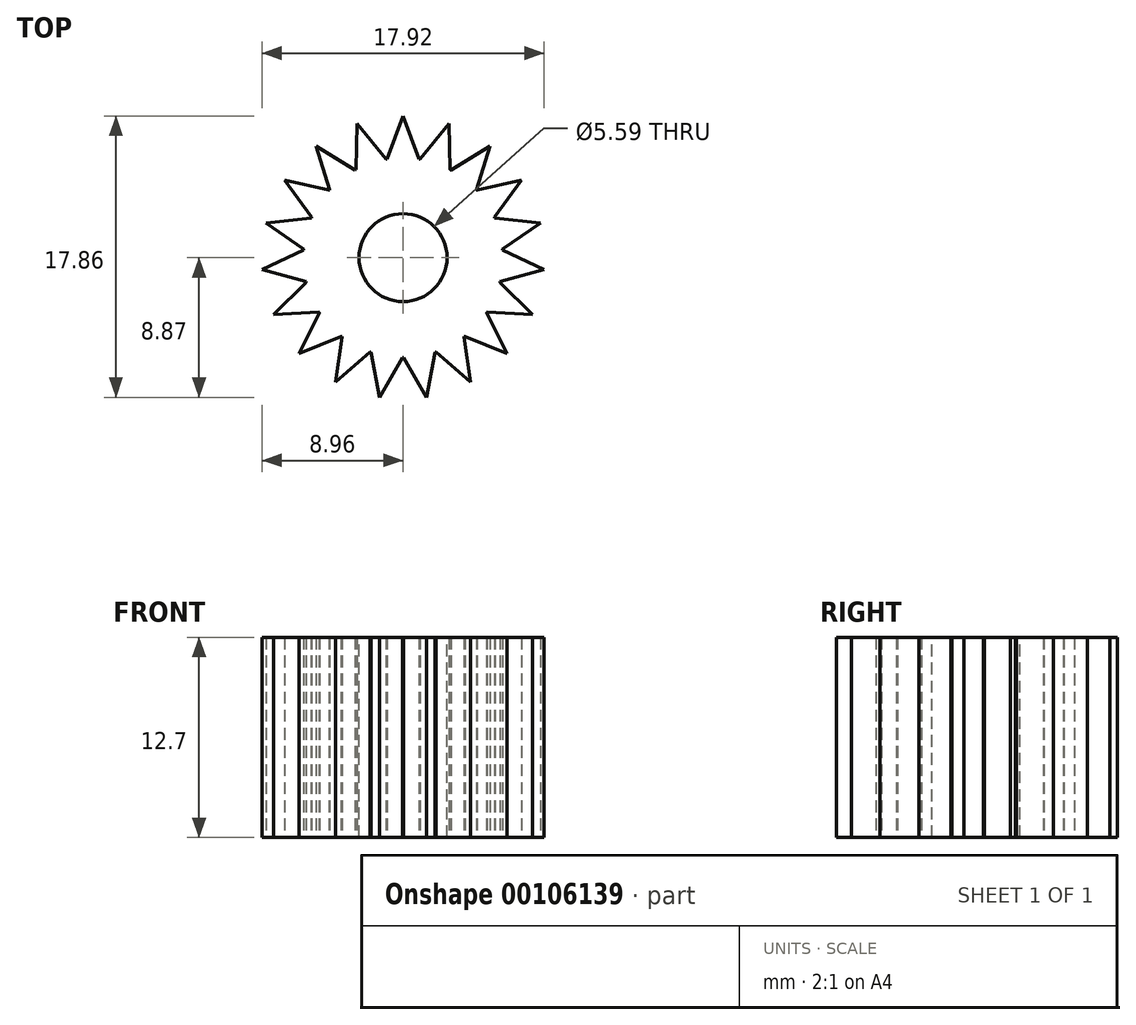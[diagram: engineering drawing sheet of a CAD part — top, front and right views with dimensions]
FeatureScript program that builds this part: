
annotation { "Feature Type Name" : "Feature", "Feature Type Description" : "" }
export const myFeature = defineFeature(function(context is Context, id is Id, definition is map)
    precondition{}
    {
        {
            var Q0;
            Q0=qCreatedBy(makeId("Top.planeOp"),FACE);
            var sketch = newSketch(context, id + "F0", { "sketchPlane" : qUnion([Q0])});
            skCircle(sketch, "E0", {"center": v(0, 0) * mm, "radius": 6.35 * mm});
            skLineSegment(sketch, "E1", {"start": v(-1.02, 6.27) * mm, "end": v(0, 9) * mm});
            skLineSegment(sketch, "E2", {"start": v(0, 9) * mm, "end": v(1.02, 6.27) * mm});
            skLineSegment(sketch, "E3.1.0", {"start": v(-3, 5.6) * mm, "end": v(-2.92, 8.5) * mm});
            skLineSegment(sketch, "E3.1.1", {"start": v(-2.92, 8.5) * mm, "end": v(-1.07, 6.26) * mm});
            skLineSegment(sketch, "E3.2.0", {"start": v(-4.65, 4.32) * mm, "end": v(-5.52, 7.1) * mm});
            skLineSegment(sketch, "E3.2.1", {"start": v(-5.52, 7.1) * mm, "end": v(-3.05, 5.57) * mm});
            skLineSegment(sketch, "E3.3.0", {"start": v(-5.8, 2.58) * mm, "end": v(-7.53, 4.92) * mm});
            skLineSegment(sketch, "E3.3.1", {"start": v(-7.53, 4.92) * mm, "end": v(-4.7, 4.28) * mm});
            skLineSegment(sketch, "E3.4.0", {"start": v(-6.33, 0.55) * mm, "end": v(-8.72, 2.2) * mm});
            skLineSegment(sketch, "E3.4.1", {"start": v(-8.72, 2.2) * mm, "end": v(-5.83, 2.52) * mm});
            skLineSegment(sketch, "E3.5.0", {"start": v(-6.16, -1.53) * mm, "end": v(-8.96, -0.74) * mm});
            skLineSegment(sketch, "E3.5.1", {"start": v(-8.96, -0.74) * mm, "end": v(-6.33, 0.5) * mm});
            skLineSegment(sketch, "E3.6.0", {"start": v(-5.33, -3.45) * mm, "end": v(-8.23, -3.61) * mm});
            skLineSegment(sketch, "E3.6.1", {"start": v(-8.23, -3.61) * mm, "end": v(-6.15, -1.59) * mm});
            skLineSegment(sketch, "E3.7.0", {"start": v(-3.92, -5) * mm, "end": v(-6.61, -6.09) * mm});
            skLineSegment(sketch, "E3.7.1", {"start": v(-6.61, -6.09) * mm, "end": v(-5.3, -3.5) * mm});
            skLineSegment(sketch, "E3.8.0", {"start": v(-2.09, -6) * mm, "end": v(-4.28, -7.9) * mm});
            skLineSegment(sketch, "E3.8.1", {"start": v(-4.28, -7.9) * mm, "end": v(-3.88, -5.03) * mm});
            skLineSegment(sketch, "E3.9.0", {"start": v(-0.03, -6.35) * mm, "end": v(-1.48, -8.87) * mm});
            skLineSegment(sketch, "E3.9.1", {"start": v(-1.48, -8.87) * mm, "end": v(-2.03, -6.02) * mm});
            skLineSegment(sketch, "E4.1.10.0", {"start": v(2.03, -6.02) * mm, "end": v(1.48, -8.87) * mm});
            skLineSegment(sketch, "E4.3.10.0", {"start": v(1.48, -8.87) * mm, "end": v(0.03, -6.35) * mm});
            skLineSegment(sketch, "E4.1.11.0", {"start": v(3.88, -5.03) * mm, "end": v(4.28, -7.9) * mm});
            skLineSegment(sketch, "E4.3.11.0", {"start": v(4.28, -7.9) * mm, "end": v(2.09, -6) * mm});
            skLineSegment(sketch, "E5.1.12.0", {"start": v(5.3, -3.5) * mm, "end": v(6.61, -6.09) * mm});
            skLineSegment(sketch, "E5.3.12.0", {"start": v(6.61, -6.09) * mm, "end": v(3.92, -5) * mm});
            skLineSegment(sketch, "E5.1.13.0", {"start": v(6.15, -1.59) * mm, "end": v(8.23, -3.61) * mm});
            skLineSegment(sketch, "E5.3.13.0", {"start": v(8.23, -3.61) * mm, "end": v(5.33, -3.45) * mm});
            skLineSegment(sketch, "E6.1.14.0", {"start": v(6.33, 0.5) * mm, "end": v(8.96, -0.74) * mm});
            skLineSegment(sketch, "E6.3.14.0", {"start": v(8.96, -0.74) * mm, "end": v(6.16, -1.53) * mm});
            skLineSegment(sketch, "E6.1.15.0", {"start": v(5.83, 2.52) * mm, "end": v(8.72, 2.2) * mm});
            skLineSegment(sketch, "E6.3.15.0", {"start": v(8.72, 2.2) * mm, "end": v(6.33, 0.55) * mm});
            skLineSegment(sketch, "E7.1.16.0", {"start": v(4.7, 4.28) * mm, "end": v(7.53, 4.92) * mm});
            skLineSegment(sketch, "E7.3.16.0", {"start": v(7.53, 4.92) * mm, "end": v(5.8, 2.58) * mm});
            skLineSegment(sketch, "E7.1.17.0", {"start": v(3.05, 5.57) * mm, "end": v(5.52, 7.1) * mm});
            skLineSegment(sketch, "E7.3.17.0", {"start": v(5.52, 7.1) * mm, "end": v(4.65, 4.32) * mm});
            skLineSegment(sketch, "E8.1.18.0", {"start": v(1.07, 6.26) * mm, "end": v(2.92, 8.5) * mm});
            skLineSegment(sketch, "E8.3.18.0", {"start": v(2.92, 8.5) * mm, "end": v(3, 5.6) * mm});
            skSolve(sketch);
        }
        {
            var Q0;
            {var subQ0=sQuery(id+"F0.wireOp",EDGE,"E0");var subQ27=makeQuery(id+"F0.imprint","INTERSECT",VERTEX,{"derivedFrom":[subQ0,sQuery(id+"F0.wireOp",EDGE,"E6.1.14.0")]});Q0=makeQuery(id+"F0.imprint","IMPRINT",FACE,{"disambiguationData":[TD([[makeQuery(id+"F0.imprint","IMPRINT",EDGE,{"disambiguationData":[TD([[subQ27,-1.0]])],"derivedFrom":subQ0}),1.0]])]});}
            var Q1;
            {var subQ0=sQuery(id+"F0.wireOp",EDGE,"E8.1.18.0");Q1=makeQuery(id+"F0.imprint","IMPRINT",FACE,{"disambiguationData":[TD([[makeQuery(id+"F0.imprint","IMPRINT",EDGE,{"derivedFrom":subQ0}),-1.0]])]});}
            var Q2;
            {var subQ0=sQuery(id+"F0.wireOp",EDGE,"E3.4.0");Q2=makeQuery(id+"F0.imprint","IMPRINT",FACE,{"disambiguationData":[TD([[makeQuery(id+"F0.imprint","IMPRINT",EDGE,{"derivedFrom":subQ0}),-1.0]])]});}
            var Q3;
            {var subQ0=sQuery(id+"F0.wireOp",EDGE,"E3.2.0");Q3=makeQuery(id+"F0.imprint","IMPRINT",FACE,{"disambiguationData":[TD([[makeQuery(id+"F0.imprint","IMPRINT",EDGE,{"derivedFrom":subQ0}),-1.0]])]});}
            var Q4;
            {var subQ0=sQuery(id+"F0.wireOp",EDGE,"E6.1.15.0");Q4=makeQuery(id+"F0.imprint","IMPRINT",FACE,{"disambiguationData":[TD([[makeQuery(id+"F0.imprint","IMPRINT",EDGE,{"derivedFrom":subQ0}),-1.0]])]});}
            var Q5;
            {var subQ0=sQuery(id+"F0.wireOp",EDGE,"E6.1.14.0");Q5=makeQuery(id+"F0.imprint","IMPRINT",FACE,{"disambiguationData":[TD([[makeQuery(id+"F0.imprint","IMPRINT",EDGE,{"derivedFrom":subQ0}),-1.0]])]});}
            var Q6;
            {var subQ0=sQuery(id+"F0.wireOp",EDGE,"E5.1.13.0");Q6=makeQuery(id+"F0.imprint","IMPRINT",FACE,{"disambiguationData":[TD([[makeQuery(id+"F0.imprint","IMPRINT",EDGE,{"derivedFrom":subQ0}),-1.0]])]});}
            var Q7;
            {var subQ0=sQuery(id+"F0.wireOp",EDGE,"E3.8.0");Q7=makeQuery(id+"F0.imprint","IMPRINT",FACE,{"disambiguationData":[TD([[makeQuery(id+"F0.imprint","IMPRINT",EDGE,{"derivedFrom":subQ0}),-1.0]])]});}
            var Q8;
            {var subQ0=sQuery(id+"F0.wireOp",EDGE,"E3.7.0");Q8=makeQuery(id+"F0.imprint","IMPRINT",FACE,{"disambiguationData":[TD([[makeQuery(id+"F0.imprint","IMPRINT",EDGE,{"derivedFrom":subQ0}),-1.0]])]});}
            var Q9;
            {var subQ0=sQuery(id+"F0.wireOp",EDGE,"E3.5.0");Q9=makeQuery(id+"F0.imprint","IMPRINT",FACE,{"disambiguationData":[TD([[makeQuery(id+"F0.imprint","IMPRINT",EDGE,{"derivedFrom":subQ0}),-1.0]])]});}
            var Q10;
            {var subQ0=sQuery(id+"F0.wireOp",EDGE,"E3.3.0");Q10=makeQuery(id+"F0.imprint","IMPRINT",FACE,{"disambiguationData":[TD([[makeQuery(id+"F0.imprint","IMPRINT",EDGE,{"derivedFrom":subQ0}),-1.0]])]});}
            var Q11;
            {var subQ0=sQuery(id+"F0.wireOp",EDGE,"E3.1.0");Q11=makeQuery(id+"F0.imprint","IMPRINT",FACE,{"disambiguationData":[TD([[makeQuery(id+"F0.imprint","IMPRINT",EDGE,{"derivedFrom":subQ0}),-1.0]])]});}
            var Q12;
            {var subQ0=sQuery(id+"F0.wireOp",EDGE,"E1");Q12=makeQuery(id+"F0.imprint","IMPRINT",FACE,{"disambiguationData":[TD([[makeQuery(id+"F0.imprint","IMPRINT",EDGE,{"derivedFrom":subQ0}),-1.0]])]});}
            var Q13;
            {var subQ0=sQuery(id+"F0.wireOp",EDGE,"E7.1.17.0");Q13=makeQuery(id+"F0.imprint","IMPRINT",FACE,{"disambiguationData":[TD([[makeQuery(id+"F0.imprint","IMPRINT",EDGE,{"derivedFrom":subQ0}),-1.0]])]});}
            var Q14;
            {var subQ0=sQuery(id+"F0.wireOp",EDGE,"E4.1.10.0");Q14=makeQuery(id+"F0.imprint","IMPRINT",FACE,{"disambiguationData":[TD([[makeQuery(id+"F0.imprint","IMPRINT",EDGE,{"derivedFrom":subQ0}),-1.0]])]});}
            var Q15;
            {var subQ0=sQuery(id+"F0.wireOp",EDGE,"E3.9.0");Q15=makeQuery(id+"F0.imprint","IMPRINT",FACE,{"disambiguationData":[TD([[makeQuery(id+"F0.imprint","IMPRINT",EDGE,{"derivedFrom":subQ0}),-1.0]])]});}
            var Q16;
            {var subQ0=sQuery(id+"F0.wireOp",EDGE,"E4.1.11.0");Q16=makeQuery(id+"F0.imprint","IMPRINT",FACE,{"disambiguationData":[TD([[makeQuery(id+"F0.imprint","IMPRINT",EDGE,{"derivedFrom":subQ0}),-1.0]])]});}
            var Q17;
            {var subQ0=sQuery(id+"F0.wireOp",EDGE,"E5.1.12.0");Q17=makeQuery(id+"F0.imprint","IMPRINT",FACE,{"disambiguationData":[TD([[makeQuery(id+"F0.imprint","IMPRINT",EDGE,{"derivedFrom":subQ0}),-1.0]])]});}
            var Q18;
            {var subQ0=sQuery(id+"F0.wireOp",EDGE,"E7.1.16.0");Q18=makeQuery(id+"F0.imprint","IMPRINT",FACE,{"disambiguationData":[TD([[makeQuery(id+"F0.imprint","IMPRINT",EDGE,{"derivedFrom":subQ0}),-1.0]])]});}
            var Q19;
            {var subQ0=sQuery(id+"F0.wireOp",EDGE,"E3.6.0");Q19=makeQuery(id+"F0.imprint","IMPRINT",FACE,{"disambiguationData":[TD([[makeQuery(id+"F0.imprint","IMPRINT",EDGE,{"derivedFrom":subQ0}),-1.0]])]});}
            extrude(context, id + "F1", {"entities" : qUnion([Q0, Q1, Q2, Q3, Q4, Q5, Q6, Q7, Q8, Q9, Q10, Q11, Q12, Q13, Q14, Q15, Q16, Q17, Q18, Q19]), "depth" : 12.7 * mm});
        }
        {
            var Q0;
            Q0=makeQuery(id+"F1.opExtrude","CAP_FACE",FACE,{"disambiguationData":[OSD([sQuery(id+"F0.wireOp",EDGE,"E0"),sQuery(id+"F0.wireOp",EDGE,"E1"),sQuery(id+"F0.wireOp",EDGE,"E2"),sQuery(id+"F0.wireOp",EDGE,"E3.1.0"),sQuery(id+"F0.wireOp",EDGE,"E3.1.1"),sQuery(id+"F0.wireOp",EDGE,"E3.2.0"),sQuery(id+"F0.wireOp",EDGE,"E3.2.1"),sQuery(id+"F0.wireOp",EDGE,"E3.3.0"),sQuery(id+"F0.wireOp",EDGE,"E3.3.1"),sQuery(id+"F0.wireOp",EDGE,"E3.4.0"),sQuery(id+"F0.wireOp",EDGE,"E3.4.1"),sQuery(id+"F0.wireOp",EDGE,"E3.5.0"),sQuery(id+"F0.wireOp",EDGE,"E3.5.1"),sQuery(id+"F0.wireOp",EDGE,"E3.6.0"),sQuery(id+"F0.wireOp",EDGE,"E3.6.1"),sQuery(id+"F0.wireOp",EDGE,"E3.7.0"),sQuery(id+"F0.wireOp",EDGE,"E3.7.1"),sQuery(id+"F0.wireOp",EDGE,"E3.8.0"),sQuery(id+"F0.wireOp",EDGE,"E3.8.1"),sQuery(id+"F0.wireOp",EDGE,"E3.9.0"),sQuery(id+"F0.wireOp",EDGE,"E3.9.1"),sQuery(id+"F0.wireOp",EDGE,"E4.1.10.0"),sQuery(id+"F0.wireOp",EDGE,"E4.3.10.0"),sQuery(id+"F0.wireOp",EDGE,"E4.1.11.0"),sQuery(id+"F0.wireOp",EDGE,"E4.3.11.0"),sQuery(id+"F0.wireOp",EDGE,"E5.1.12.0"),sQuery(id+"F0.wireOp",EDGE,"E5.3.12.0"),sQuery(id+"F0.wireOp",EDGE,"E5.1.13.0"),sQuery(id+"F0.wireOp",EDGE,"E5.3.13.0"),sQuery(id+"F0.wireOp",EDGE,"E6.1.14.0"),sQuery(id+"F0.wireOp",EDGE,"E6.3.14.0"),sQuery(id+"F0.wireOp",EDGE,"E6.1.15.0"),sQuery(id+"F0.wireOp",EDGE,"E6.3.15.0"),sQuery(id+"F0.wireOp",EDGE,"E7.1.16.0"),sQuery(id+"F0.wireOp",EDGE,"E7.3.16.0"),sQuery(id+"F0.wireOp",EDGE,"E7.1.17.0"),sQuery(id+"F0.wireOp",EDGE,"E7.3.17.0"),sQuery(id+"F0.wireOp",EDGE,"E8.1.18.0"),sQuery(id+"F0.wireOp",EDGE,"E8.3.18.0")])],"isStart":false});
            var sketch = newSketch(context, id + "F2", { "sketchPlane" : qUnion([Q0])});
            skCircle(sketch, "E9", {"center": v(0, 0) * mm, "radius": 2.8 * mm});
            skSolve(sketch);
        }
        {
            var Q0;
            Q0=makeQuery(id+"F2.imprint","IMPRINT",FACE,{"disambiguationData":[TD([[makeQuery(id+"F2.imprint","IMPRINT",EDGE,{"derivedFrom":sQuery(id+"F2.wireOp",EDGE,"E9")}),1.0]])]});
            extrude(context, id + "F3", {"entities" : qUnion([Q0]), "operationType" : NewBodyOperationType.REMOVE, "oppositeDirection" : true, "depth" : 12.7 * mm});
        }
    });
